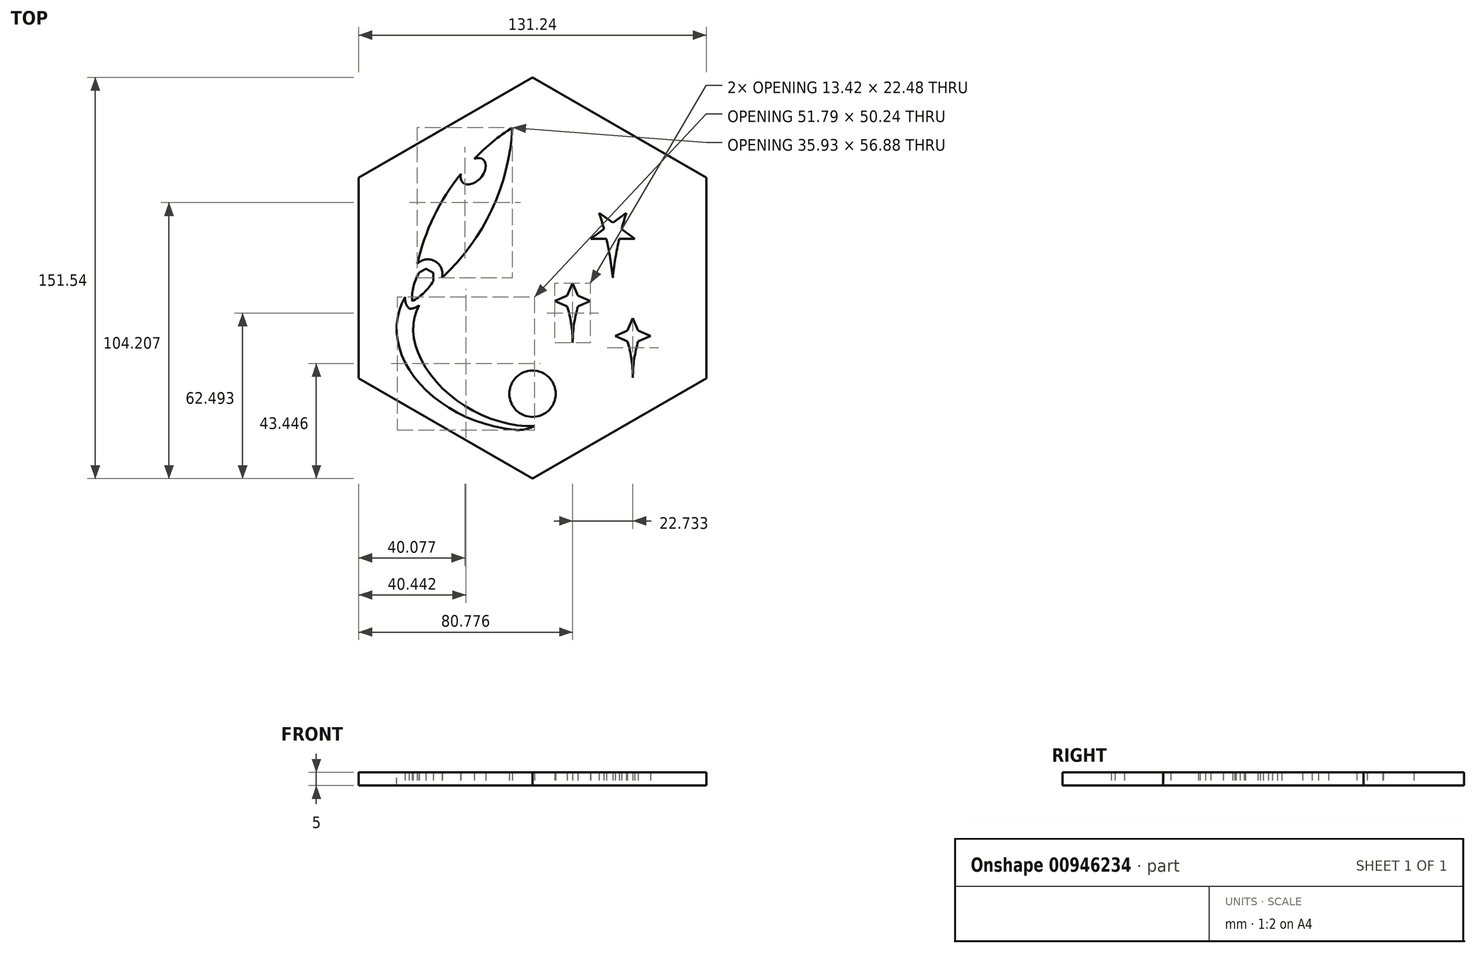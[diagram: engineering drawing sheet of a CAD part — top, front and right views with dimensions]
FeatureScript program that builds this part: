
annotation { "Feature Type Name" : "Feature", "Feature Type Description" : "" }
export const myFeature = defineFeature(function(context is Context, id is Id, definition is map)
    precondition{}
    {
        {
            var Q0;
            Q0=qCreatedBy(makeId("Top.planeOp"),FACE);
            var sketch = newSketch(context, id + "F0", { "sketchPlane" : qUnion([Q0])});
            skCircle(sketch, "E0.cCircle", {"center": v(0, 0) * mm, "radius": 60.62 * mm, "construction": true});
            skLineSegment(sketch, "E0.0", {"start": v(60.62, 35) * mm, "end": v(60.62, -35) * mm});
            skLineSegment(sketch, "E0.1", {"start": v(60.62, -35) * mm, "end": v(0, -70) * mm});
            skLineSegment(sketch, "E0.2", {"start": v(0, -70) * mm, "end": v(-60.62, -35) * mm});
            skLineSegment(sketch, "E0.3", {"start": v(-60.62, -35) * mm, "end": v(-60.62, 35) * mm});
            skLineSegment(sketch, "E0.4", {"start": v(-60.62, 35) * mm, "end": v(0, 70) * mm});
            skLineSegment(sketch, "E0.5", {"start": v(0, 70) * mm, "end": v(60.62, 35) * mm});
            skPoint(sketch, "E0.0.midPoint", {"position": v(60.62, 0) * mm});
            skLineSegment(sketch, "E1", {"start": v(0, 0) * mm, "end": v(0, -35) * mm, "construction": true});
            skLineSegment(sketch, "E2", {"start": v(-30.31, 17.5) * mm, "end": v(-60.62, 35) * mm, "construction": true});
            skLineSegment(sketch, "E3", {"start": v(0, 0) * mm, "end": v(60.62, 35) * mm, "construction": true});
            skLineSegment(sketch, "E4", {"start": v(60.62, -35) * mm, "end": v(15.16, -8.75) * mm, "construction": true});
            skLineSegment(sketch, "E5", {"start": v(0, -35) * mm, "end": v(30.31, 17.5) * mm, "construction": true});
            skLineSegment(sketch, "E6", {"start": v(0, -35) * mm, "end": v(0, -43.75) * mm, "construction": true});
            skLineSegment(sketch, "E7", {"start": v(0, -52.5) * mm, "end": v(0, -70) * mm, "construction": true});
            skLineSegment(sketch, "E8", {"start": v(0, -43.75) * mm, "end": v(0, -52.5) * mm, "construction": true});
            skCircle(sketch, "E9", {"center": v(0, -43.75) * mm, "radius": 8.75 * mm});
            skPoint(sketch, "E10", {"position": v(37.89, -21.88) * mm});
            skPoint(sketch, "E11", {"position": v(-30.31, 17.5) * mm});
            skLineSegment(sketch, "E12", {"start": v(-60.62, -35) * mm, "end": v(-45.47, -8.75) * mm, "construction": true});
            skLineSegment(sketch, "E13", {"start": v(0, 70) * mm, "end": v(-7.58, 56.88) * mm, "construction": true});
            skLineSegment(sketch, "E14", {"start": v(-45.47, -8.75) * mm, "end": v(-37.89, 4.37) * mm, "construction": true});
            skLineSegment(sketch, "E15", {"start": v(-15.16, 43.75) * mm, "end": v(-30.31, 17.5) * mm, "construction": true});
            skLineSegment(sketch, "E16", {"start": v(-7.58, 56.88) * mm, "end": v(-15.16, 43.75) * mm, "construction": true});
            skArc(sketch, "E17", {"start": v(-60.62, -16.52) * mm, "mid": v(-59.59, -16.11) * mm, "end": v(-58.56, -15.69) * mm, "construction": true});
            skLineSegment(sketch, "E18", {"start": v(-15.16, 8.75) * mm, "end": v(-30.31, 17.5) * mm, "construction": true});
            skLineSegment(sketch, "E19", {"start": v(0, 0) * mm, "end": v(-15.16, 8.75) * mm, "construction": true});
            skPoint(sketch, "E20", {"position": v(-22.73, 13.12) * mm});
            skArc(sketch, "E21.trimOffspring", {"start": v(-45.47, -8.75) * mm, "mid": v(-18.65, 19.52) * mm, "end": v(-7.58, 56.88) * mm});
            skArc(sketch, "E22.MirrorCS", {"start": v(-45.47, -8.75) * mm, "mid": v(-34.4, 28.6) * mm, "end": v(-7.58, 56.88) * mm});
            skLineSegment(sketch, "E23", {"start": v(-37.89, 4.37) * mm, "end": v(-34.1, 10.94) * mm, "construction": true});
            skLineSegment(sketch, "E24", {"start": v(-34.1, 10.94) * mm, "end": v(-30.31, 17.5) * mm, "construction": true});
            skCircle(sketch, "E25.cCircle", {"center": v(30.31, 17.5) * mm, "radius": 2.7 * mm, "construction": true});
            skLineSegment(sketch, "E25.0", {"start": v(35.45, 24.58) * mm, "end": v(30.31, 8.75) * mm});
            skLineSegment(sketch, "E25.1", {"start": v(38.63, 14.8) * mm, "end": v(21.99, 14.8) * mm});
            skLineSegment(sketch, "E25.2", {"start": v(30.31, 8.75) * mm, "end": v(25.17, 24.58) * mm});
            skLineSegment(sketch, "E25.3", {"start": v(21.99, 14.8) * mm, "end": v(35.45, 24.58) * mm});
            skLineSegment(sketch, "E25.4", {"start": v(25.17, 24.58) * mm, "end": v(38.63, 14.8) * mm});
            skPoint(sketch, "E25.0.midPoint", {"position": v(32.88, 16.66) * mm});
            skPoint(sketch, "E26.orphan", {"position": v(27.13, 18.53) * mm});
            skPoint(sketch, "E27.orphan", {"position": v(30.31, 20.84) * mm});
            skPoint(sketch, "E28.orphan", {"position": v(33.49, 18.53) * mm});
            skPoint(sketch, "E29.orphan", {"position": v(32.28, 14.8) * mm});
            skPoint(sketch, "E30.orphan", {"position": v(28.35, 14.8) * mm});
            skLineSegment(sketch, "E31", {"start": v(30.31, 17.5) * mm, "end": v(30.31, 0) * mm, "construction": true});
            skPoint(sketch, "E32", {"position": v(30.31, 8.75) * mm});
            skArc(sketch, "E33", {"start": v(30.31, 0) * mm, "mid": v(28.4, 12.43) * mm, "end": v(25.17, 24.58) * mm});
            skArc(sketch, "E34", {"start": v(35.45, 24.58) * mm, "mid": v(32.22, 12.43) * mm, "end": v(30.31, 0) * mm});
            skLineSegment(sketch, "E35", {"start": v(30.31, 17.5) * mm, "end": v(27.97, 18.85) * mm, "construction": true});
            skCircle(sketch, "E36", {"center": v(30.31, 17.5) * mm, "radius": 1.35 * mm, "construction": true});
            skPoint(sketch, "E37", {"position": v(29.14, 18.18) * mm});
            skCircle(sketch, "E38", {"center": v(30.31, 17.5) * mm, "radius": 2.03 * mm, "construction": true});
            skLineSegment(sketch, "E39", {"start": v(30.31, 17.5) * mm, "end": v(30.99, 18.67) * mm, "construction": true});
            skLineSegment(sketch, "E40", {"start": v(30.99, 18.67) * mm, "end": v(31.66, 19.84) * mm, "construction": true});
            skPoint(sketch, "E41", {"position": v(31.32, 19.26) * mm});
            skSolve(sketch);
        }
        {
            var Q0;
            Q0=qCreatedBy(makeId("Top.planeOp"),FACE);
            var sketch = newSketch(context, id + "F1", { "sketchPlane" : qUnion([Q0])});
            skPoint(sketch, "E42.0", {"position": v(15.16, -8.75) * mm});
            skLineSegment(sketch, "E43.0", {"start": v(0, -70) * mm, "end": v(-60.62, -35) * mm});
            skLineSegment(sketch, "E44.0", {"start": v(-60.62, -35) * mm, "end": v(-60.62, 35) * mm});
            skLineSegment(sketch, "E45.0", {"start": v(-60.62, 35) * mm, "end": v(0, 70) * mm});
            skLineSegment(sketch, "E46.0", {"start": v(0, 70) * mm, "end": v(60.62, 35) * mm});
            skLineSegment(sketch, "E47.0", {"start": v(60.62, 35) * mm, "end": v(60.62, -35) * mm});
            skLineSegment(sketch, "E48.0", {"start": v(60.62, -35) * mm, "end": v(0, -70) * mm});
            skArc(sketch, "E49.0", {"start": v(-45.47, -8.75) * mm, "mid": v(-18.65, 19.52) * mm, "end": v(-7.58, 56.88) * mm});
            skArc(sketch, "E50.0", {"start": v(-45.47, -8.75) * mm, "mid": v(-34.4, 28.6) * mm, "end": v(-7.58, 56.88) * mm});
            skCircle(sketch, "E51.cCircle", {"center": v(15.16, -8.75) * mm, "radius": 2.03 * mm, "construction": true});
            skLineSegment(sketch, "E51.3", {"start": v(13.13, -6.72) * mm, "end": v(17.18, -6.72) * mm});
            skPoint(sketch, "E51.0.midPoint", {"position": v(17.18, -8.75) * mm});
            skCircle(sketch, "E52.cCircle", {"center": v(15.16, -5.55) * mm, "radius": 1.17 * mm, "construction": true});
            skLineSegment(sketch, "E52.1", {"start": v(13.13, -6.72) * mm, "end": v(15.16, -3.2) * mm});
            skLineSegment(sketch, "E52.2", {"start": v(15.16, -3.2) * mm, "end": v(17.18, -6.72) * mm});
            skPoint(sketch, "E52.0.midPoint", {"position": v(15.16, -6.72) * mm});
            skLineSegment(sketch, "E53", {"start": v(15.16, -5.55) * mm, "end": v(15.16, -0.87) * mm, "construction": true});
            skPoint(sketch, "E54", {"position": v(15.16, -3.2) * mm});
            skLineSegment(sketch, "E55", {"start": v(15.16, -3.2) * mm, "end": v(15.16, -0.87) * mm, "construction": true});
            skLineSegment(sketch, "E56", {"start": v(17.18, -6.72) * mm, "end": v(15.16, -2.04) * mm});
            skLineSegment(sketch, "E57", {"start": v(13.13, -6.72) * mm, "end": v(15.16, -2.04) * mm});
            skLineSegment(sketch, "E58.1.0", {"start": v(13.13, -6.72) * mm, "end": v(8.44, -8.75) * mm});
            skPoint(sketch, "E58.1.1", {"position": v(13.13, -8.75) * mm});
            skLineSegment(sketch, "E58.1.2", {"start": v(9.62, -8.75) * mm, "end": v(13.13, -6.72) * mm});
            skLineSegment(sketch, "E58.1.3", {"start": v(9.62, -8.75) * mm, "end": v(7.27, -8.75) * mm, "construction": true});
            skLineSegment(sketch, "E58.1.4", {"start": v(11.96, -8.75) * mm, "end": v(7.27, -8.75) * mm, "construction": true});
            skLineSegment(sketch, "E58.1.5", {"start": v(13.13, -10.78) * mm, "end": v(8.44, -8.75) * mm});
            skLineSegment(sketch, "E58.1.6", {"start": v(13.13, -10.78) * mm, "end": v(13.13, -6.72) * mm});
            skCircle(sketch, "E58.1.7", {"center": v(11.96, -8.75) * mm, "radius": 1.17 * mm, "construction": true});
            skPoint(sketch, "E58.1.8", {"position": v(9.62, -8.75) * mm});
            skLineSegment(sketch, "E58.1.9", {"start": v(13.13, -10.78) * mm, "end": v(9.62, -8.75) * mm});
            skLineSegment(sketch, "E58.2.0", {"start": v(13.13, -10.78) * mm, "end": v(15.16, -15.46) * mm});
            skPoint(sketch, "E58.2.1", {"position": v(15.16, -10.78) * mm});
            skLineSegment(sketch, "E58.2.2", {"start": v(15.16, -14.3) * mm, "end": v(13.13, -10.78) * mm});
            skLineSegment(sketch, "E58.2.3", {"start": v(15.16, -14.3) * mm, "end": v(15.16, -16.63) * mm, "construction": true});
            skLineSegment(sketch, "E58.2.4", {"start": v(15.16, -11.95) * mm, "end": v(15.16, -16.63) * mm, "construction": true});
            skLineSegment(sketch, "E58.2.5", {"start": v(17.18, -10.78) * mm, "end": v(15.16, -15.46) * mm});
            skLineSegment(sketch, "E58.2.6", {"start": v(17.18, -10.78) * mm, "end": v(13.13, -10.78) * mm});
            skCircle(sketch, "E58.2.7", {"center": v(15.16, -11.95) * mm, "radius": 1.17 * mm, "construction": true});
            skPoint(sketch, "E58.2.8", {"position": v(15.16, -14.3) * mm});
            skLineSegment(sketch, "E58.2.9", {"start": v(17.18, -10.78) * mm, "end": v(15.16, -14.3) * mm});
            skLineSegment(sketch, "E58.3.0", {"start": v(17.18, -10.78) * mm, "end": v(21.87, -8.75) * mm});
            skLineSegment(sketch, "E58.3.2", {"start": v(20.7, -8.75) * mm, "end": v(17.18, -10.78) * mm});
            skLineSegment(sketch, "E58.3.3", {"start": v(20.7, -8.75) * mm, "end": v(23.04, -8.75) * mm, "construction": true});
            skLineSegment(sketch, "E58.3.4", {"start": v(18.35, -8.75) * mm, "end": v(23.04, -8.75) * mm, "construction": true});
            skLineSegment(sketch, "E58.3.5", {"start": v(17.18, -6.72) * mm, "end": v(21.87, -8.75) * mm});
            skLineSegment(sketch, "E58.3.6", {"start": v(17.18, -6.72) * mm, "end": v(17.18, -10.78) * mm});
            skCircle(sketch, "E58.3.7", {"center": v(18.35, -8.75) * mm, "radius": 1.17 * mm, "construction": true});
            skPoint(sketch, "E58.3.8", {"position": v(20.7, -8.75) * mm});
            skLineSegment(sketch, "E58.3.9", {"start": v(17.18, -6.72) * mm, "end": v(20.7, -8.75) * mm});
            skLineSegment(sketch, "E59", {"start": v(15.16, -8.75) * mm, "end": v(15.16, -24.51) * mm, "construction": true});
            skArc(sketch, "E60", {"start": v(17.18, -10.78) * mm, "mid": v(15.67, -17.57) * mm, "end": v(15.16, -24.51) * mm});
            skArc(sketch, "E61", {"start": v(15.16, -24.51) * mm, "mid": v(14.65, -17.57) * mm, "end": v(13.13, -10.78) * mm});
            skPoint(sketch, "E62.0", {"position": v(37.89, -21.88) * mm});
            skCircle(sketch, "E63.cCircle", {"center": v(37.89, -21.88) * mm, "radius": 2.03 * mm, "construction": true});
            skLineSegment(sketch, "E63.0", {"start": v(39.92, -19.85) * mm, "end": v(39.92, -23.9) * mm});
            skLineSegment(sketch, "E63.1", {"start": v(39.92, -23.9) * mm, "end": v(35.86, -23.9) * mm});
            skLineSegment(sketch, "E63.2", {"start": v(35.86, -23.9) * mm, "end": v(35.86, -19.85) * mm});
            skLineSegment(sketch, "E63.3", {"start": v(35.86, -19.85) * mm, "end": v(39.92, -19.85) * mm});
            skPoint(sketch, "E63.0.midPoint", {"position": v(39.92, -21.88) * mm});
            skCircle(sketch, "E64.cCircle", {"center": v(37.89, -18.68) * mm, "radius": 1.17 * mm, "construction": true});
            skLineSegment(sketch, "E64.0", {"start": v(35.86, -19.85) * mm, "end": v(37.89, -16.33) * mm});
            skLineSegment(sketch, "E64.1", {"start": v(37.89, -16.33) * mm, "end": v(39.92, -19.85) * mm});
            skLineSegment(sketch, "E64.2", {"start": v(39.92, -19.85) * mm, "end": v(35.86, -19.85) * mm});
            skPoint(sketch, "E64.0.midPoint", {"position": v(36.87, -18.1) * mm});
            skLineSegment(sketch, "E65", {"start": v(37.89, -18.68) * mm, "end": v(37.89, -14) * mm, "construction": true});
            skLineSegment(sketch, "E66", {"start": v(37.89, -16.33) * mm, "end": v(37.89, -14) * mm, "construction": true});
            skLineSegment(sketch, "E67", {"start": v(39.92, -19.85) * mm, "end": v(37.89, -15.16) * mm});
            skLineSegment(sketch, "E68", {"start": v(35.86, -19.85) * mm, "end": v(37.89, -15.16) * mm});
            skLineSegment(sketch, "E69.1.0", {"start": v(35.86, -23.9) * mm, "end": v(32.35, -21.87) * mm});
            skLineSegment(sketch, "E69.1.1", {"start": v(34.69, -21.87) * mm, "end": v(30, -21.88) * mm, "construction": true});
            skLineSegment(sketch, "E69.1.2", {"start": v(32.35, -21.88) * mm, "end": v(35.86, -19.85) * mm});
            skLineSegment(sketch, "E69.1.3", {"start": v(32.35, -21.88) * mm, "end": v(30, -21.88) * mm, "construction": true});
            skLineSegment(sketch, "E69.1.4", {"start": v(35.86, -23.9) * mm, "end": v(31.18, -21.88) * mm});
            skPoint(sketch, "E69.1.5", {"position": v(34.1, -22.89) * mm});
            skLineSegment(sketch, "E69.1.6", {"start": v(35.86, -19.85) * mm, "end": v(35.86, -23.9) * mm});
            skCircle(sketch, "E69.1.7", {"center": v(34.69, -21.87) * mm, "radius": 1.17 * mm, "construction": true});
            skLineSegment(sketch, "E69.1.8", {"start": v(35.86, -19.85) * mm, "end": v(31.18, -21.88) * mm});
            skLineSegment(sketch, "E69.2.0", {"start": v(39.92, -23.9) * mm, "end": v(37.89, -27.42) * mm});
            skLineSegment(sketch, "E69.2.1", {"start": v(37.89, -25.07) * mm, "end": v(37.89, -29.76) * mm, "construction": true});
            skLineSegment(sketch, "E69.2.2", {"start": v(37.89, -27.42) * mm, "end": v(35.86, -23.9) * mm});
            skLineSegment(sketch, "E69.2.3", {"start": v(37.89, -27.42) * mm, "end": v(37.89, -29.76) * mm, "construction": true});
            skLineSegment(sketch, "E69.2.4", {"start": v(39.92, -23.9) * mm, "end": v(37.89, -28.59) * mm});
            skPoint(sketch, "E69.2.5", {"position": v(38.9, -25.66) * mm});
            skLineSegment(sketch, "E69.2.6", {"start": v(35.86, -23.9) * mm, "end": v(39.92, -23.9) * mm});
            skCircle(sketch, "E69.2.7", {"center": v(37.89, -25.07) * mm, "radius": 1.17 * mm, "construction": true});
            skLineSegment(sketch, "E69.2.8", {"start": v(35.86, -23.9) * mm, "end": v(37.89, -28.59) * mm});
            skLineSegment(sketch, "E69.3.0", {"start": v(39.92, -19.85) * mm, "end": v(43.43, -21.88) * mm});
            skLineSegment(sketch, "E69.3.1", {"start": v(41.09, -21.88) * mm, "end": v(45.77, -21.87) * mm, "construction": true});
            skLineSegment(sketch, "E69.3.2", {"start": v(43.43, -21.87) * mm, "end": v(39.92, -23.9) * mm});
            skLineSegment(sketch, "E69.3.3", {"start": v(43.43, -21.87) * mm, "end": v(45.77, -21.87) * mm, "construction": true});
            skLineSegment(sketch, "E69.3.4", {"start": v(39.92, -19.85) * mm, "end": v(44.6, -21.88) * mm});
            skPoint(sketch, "E69.3.5", {"position": v(41.67, -20.86) * mm});
            skLineSegment(sketch, "E69.3.6", {"start": v(39.92, -23.9) * mm, "end": v(39.92, -19.85) * mm});
            skCircle(sketch, "E69.3.7", {"center": v(41.09, -21.88) * mm, "radius": 1.17 * mm, "construction": true});
            skLineSegment(sketch, "E69.3.8", {"start": v(39.92, -23.9) * mm, "end": v(44.6, -21.87) * mm});
            skLineSegment(sketch, "E70", {"start": v(37.89, -21.88) * mm, "end": v(37.89, -37.64) * mm, "construction": true});
            skSolve(sketch);
        }
        {
            var Q0;
            Q0=makeQuery(id+"F0.imprint","IMPRINT",FACE,{"disambiguationData":[TD([[makeQuery(id+"F0.imprint","IMPRINT",EDGE,{"derivedFrom":sQuery(id+"F0.wireOp",EDGE,"E0.0")}),-1.0]])]});
            var sketch = newSketch(context, id + "F2", { "sketchPlane" : qUnion([Q0])});
            skPoint(sketch, "E71.0", {"position": v(35.86, -23.9) * mm});
            skPoint(sketch, "E72.0", {"position": v(39.92, -23.9) * mm});
            skPoint(sketch, "E73.0", {"position": v(37.89, -37.64) * mm});
            skArc(sketch, "E74", {"start": v(37.89, -37.64) * mm, "mid": v(37.38, -30.7) * mm, "end": v(35.86, -23.9) * mm});
            skLineSegment(sketch, "E75.0", {"start": v(37.89, -21.88) * mm, "end": v(37.89, -37.64) * mm, "construction": true});
            skArc(sketch, "E76", {"start": v(39.92, -23.9) * mm, "mid": v(38.4, -30.7) * mm, "end": v(37.89, -37.64) * mm});
            skSolve(sketch);
        }
        {
            var Q0;
            Q0=makeQuery(id+"F0.imprint","IMPRINT",FACE,{"disambiguationData":[TD([[makeQuery(id+"F0.imprint","IMPRINT",EDGE,{"derivedFrom":sQuery(id+"F0.wireOp",EDGE,"E0.0")}),-1.0]])]});
            var sketch = newSketch(context, id + "F3", { "sketchPlane" : qUnion([Q0])});
            skArc(sketch, "E77.0", {"start": v(-43.5, 5.36) * mm, "mid": v(-30.57, 34.63) * mm, "end": v(-7.58, 56.88) * mm});
            skArc(sketch, "E77.1", {"start": v(-34.23, 0) * mm, "mid": v(-15.35, 25.84) * mm, "end": v(-7.58, 56.88) * mm});
            skArc(sketch, "E78", {"start": v(-34.23, 0) * mm, "mid": v(-36.78, 6.3) * mm, "end": v(-43.5, 5.36) * mm});
            skLineSegment(sketch, "E79", {"start": v(-34.23, 0) * mm, "end": v(-36.55, 1.34) * mm, "construction": true});
            skLineSegment(sketch, "E80", {"start": v(-38.87, 2.68) * mm, "end": v(-43.5, 5.36) * mm, "construction": true});
            skLineSegment(sketch, "E81", {"start": v(-36.55, 1.34) * mm, "end": v(-38.87, 2.68) * mm, "construction": true});
            skLineSegment(sketch, "E82", {"start": v(-38.87, 2.68) * mm, "end": v(-40.2, 0.36) * mm, "construction": true});
            skPoint(sketch, "E83.orphan", {"position": v(-45.47, -8.75) * mm});
            skCircle(sketch, "E84.cCircle", {"center": v(-40.2, 0.36) * mm, "radius": 2.68 * mm, "construction": true});
            skLineSegment(sketch, "E84.2", {"start": v(-42.89, 1.9) * mm, "end": v(-40.2, 3.45) * mm});
            skLineSegment(sketch, "E84.3", {"start": v(-40.2, 3.45) * mm, "end": v(-37.53, 1.9) * mm});
            skLineSegment(sketch, "E84.4", {"start": v(-37.53, 1.9) * mm, "end": v(-37.53, -1.19) * mm});
            skPoint(sketch, "E84.0.midPoint", {"position": v(-41.55, -1.96) * mm});
            skArc(sketch, "E85", {"start": v(-45.47, -8.75) * mm, "mid": v(-40.95, -5.54) * mm, "end": v(-37.53, -1.19) * mm, "construction": true});
            skArc(sketch, "E86.MirrorCS", {"start": v(-45.47, -8.75) * mm, "mid": v(-44.94, -3.24) * mm, "end": v(-42.89, 1.9) * mm, "construction": true});
            skLineSegment(sketch, "E87", {"start": v(-36.22, 1.9) * mm, "end": v(-42.37, -8.75) * mm, "construction": true});
            skLineSegment(sketch, "E88", {"start": v(-35.74, 1.9) * mm, "end": v(-41.9, -8.75) * mm, "construction": true});
            skCircle(sketch, "E89.0", {"center": v(0, -43.75) * mm, "radius": 8.75 * mm});
            skLineSegment(sketch, "E90", {"start": v(0, -43.75) * mm, "end": v(-8.75, -43.75) * mm, "construction": true});
            skLineSegment(sketch, "E91", {"start": v(-17.5, -43.75) * mm, "end": v(-8.75, -43.75) * mm, "construction": true});
            skPoint(sketch, "E92", {"position": v(-44.94, -3.24) * mm});
            skPoint(sketch, "E93", {"position": v(-40.95, -5.54) * mm});
            skLineSegment(sketch, "E94", {"start": v(-48.15, -7.2) * mm, "end": v(-45.47, -8.75) * mm, "construction": true});
            skLineSegment(sketch, "E95", {"start": v(-37.53, -1.19) * mm, "end": v(-42.79, -10.3) * mm, "construction": true});
            skLineSegment(sketch, "E96", {"start": v(0, -43.75) * mm, "end": v(0, -52.5) * mm, "construction": true});
            skLineSegment(sketch, "E97", {"start": v(0, -43.75) * mm, "end": v(-6.19, -49.94) * mm, "construction": true});
            skLineSegment(sketch, "E98", {"start": v(0, -52.5) * mm, "end": v(-8.75, -43.75) * mm, "construction": true});
            skPoint(sketch, "E99", {"position": v(-4.38, -48.13) * mm});
            skLineSegment(sketch, "E100", {"start": v(0, -43.75) * mm, "end": v(-16.17, -50.45) * mm, "construction": true});
            skLineSegment(sketch, "E101", {"start": v(-6.19, -49.94) * mm, "end": v(-8.75, -43.75) * mm, "construction": true});
            skPoint(sketch, "E102", {"position": v(-7.47, -46.84) * mm});
            skCircle(sketch, "E103", {"center": v(0, -43.75) * mm, "radius": 17.5 * mm, "construction": true});
            skLineSegment(sketch, "E104", {"start": v(-16.17, -50.45) * mm, "end": v(-16.83, -47.1) * mm, "construction": true});
            skPoint(sketch, "E105", {"position": v(-16.83, -47.1) * mm});
            skLineSegment(sketch, "E106", {"start": v(0, -43.75) * mm, "end": v(-12.63, -46.26) * mm, "construction": true});
            skLineSegment(sketch, "E107", {"start": v(-45.47, -8.75) * mm, "end": v(-44.94, -3.24) * mm, "construction": true});
            skLineSegment(sketch, "E108", {"start": v(-40.95, -5.54) * mm, "end": v(-45.47, -8.75) * mm, "construction": true});
            skPoint(sketch, "E109", {"position": v(-45.2, -6) * mm});
            skPoint(sketch, "E110", {"position": v(-43.2, -7.15) * mm});
            skLineSegment(sketch, "E111", {"start": v(-13.13, -43.75) * mm, "end": v(-12.63, -46.26) * mm, "construction": true});
            skPoint(sketch, "E112.0", {"position": v(-15.16, 43.75) * mm});
            skPoint(sketch, "E113.0", {"position": v(-30.31, 17.5) * mm});
            skLineSegment(sketch, "E114", {"start": v(-15.16, 43.75) * mm, "end": v(-18.94, 37.19) * mm, "construction": true});
            skLineSegment(sketch, "E115", {"start": v(-22.73, 30.62) * mm, "end": v(-30.31, 17.5) * mm, "construction": true});
            skLineSegment(sketch, "E116", {"start": v(-18.94, 37.19) * mm, "end": v(-22.73, 30.62) * mm, "construction": true});
            skEllipse(sketch, "E117", {"center": v(-22.42, 40.3) * mm, "majorRadius": 5.8 * mm, "minorRadius": 4.67 * mm, "majorAxis": v(0.67, 0.74), "construction": true});
            skPoint(sketch, "E118", {"position": v(-26.3, 35.97) * mm});
            skPoint(sketch, "E119", {"position": v(-18.55, 44.63) * mm});
            skLineSegment(sketch, "E120", {"start": v(-7.58, 56.88) * mm, "end": v(-27.47, 31.17) * mm, "construction": true});
            skEllipse(sketch, "E121", {"center": v(-22.73, 30.62) * mm, "majorRadius": 8.74 * mm, "minorRadius": 3.79 * mm, "majorAxis": v(0.87, -0.5), "construction": true});
            skPoint(sketch, "E122", {"position": v(-24.63, 27.34) * mm});
            skPoint(sketch, "E123", {"position": v(-30.3, 35) * mm});
            skLineSegment(sketch, "E124", {"start": v(-30.3, 35) * mm, "end": v(-27.47, 31.17) * mm, "construction": true});
            skPoint(sketch, "E125", {"position": v(-27.47, 31.17) * mm});
            skPoint(sketch, "E126", {"position": v(-20.84, 33.9) * mm});
            skPoint(sketch, "E127", {"position": v(-25.9, 43.42) * mm});
            skLineSegment(sketch, "E128", {"start": v(-27.47, 31.17) * mm, "end": v(-24.63, 27.34) * mm, "construction": true});
            skPoint(sketch, "E129", {"position": v(-28.89, 33.08) * mm});
            skLineSegment(sketch, "E130", {"start": v(-7.58, 56.88) * mm, "end": v(-28.89, 33.08) * mm, "construction": true});
            skPoint(sketch, "E131", {"position": v(-18.94, 37.19) * mm});
            skLineSegment(sketch, "E132", {"start": v(-45.47, -8.75) * mm, "end": v(-42.79, -10.3) * mm, "construction": true});
            skLineSegment(sketch, "E133", {"start": v(-16.83, -47.1) * mm, "end": v(-17.5, -43.75) * mm, "construction": true});
            skPoint(sketch, "E134", {"position": v(-17.17, -45.42) * mm});
            skPoint(sketch, "E135", {"position": v(-12.88, -45) * mm});
            skLineSegment(sketch, "E136", {"start": v(-12.88, -45) * mm, "end": v(-17.17, -45.42) * mm, "construction": true});
            skLineSegment(sketch, "E137", {"start": v(-12.63, -46.26) * mm, "end": v(-17.16, -47.16) * mm, "construction": true});
            skLineSegment(sketch, "E138", {"start": v(-13.13, -43.75) * mm, "end": v(-17.5, -43.75) * mm, "construction": true});
            skPoint(sketch, "E139", {"position": v(-15.31, -43.75) * mm});
            skPoint(sketch, "E140", {"position": v(-14.9, -46.71) * mm});
            skLineSegment(sketch, "E141", {"start": v(-14.9, -46.71) * mm, "end": v(-15.02, -45.21) * mm, "construction": true});
            skPoint(sketch, "E142", {"position": v(-14.96, -45.96) * mm});
            skArc(sketch, "E143", {"start": v(-17.17, -45.42) * mm, "mid": v(-16.01, -45.5) * mm, "end": v(-14.96, -45.96) * mm, "construction": true});
            skArc(sketch, "E144", {"start": v(-16.83, -47.1) * mm, "mid": v(-15.8, -46.7) * mm, "end": v(-14.96, -45.96) * mm, "construction": true});
            skPoint(sketch, "E145", {"position": v(-40.3, -35.38) * mm});
            skLineSegment(sketch, "E146", {"start": v(-40.3, -35.38) * mm, "end": v(-43.78, -37.93) * mm, "construction": true});
            skPoint(sketch, "E147", {"position": v(-42.04, -36.66) * mm});
            skArc(sketch, "E148", {"start": v(-45.47, -8.75) * mm, "mid": v(-41.85, -36.9) * mm, "end": v(-14.96, -45.96) * mm, "construction": true});
            skLineSegment(sketch, "E149", {"start": v(-46.6, -11.63) * mm, "end": v(-45.47, -8.75) * mm, "construction": true});
            skLineSegment(sketch, "E150", {"start": v(-45.47, -8.75) * mm, "end": v(-46.49, -5.83) * mm, "construction": true});
            skArc(sketch, "E151", {"start": v(-48.15, -7.2) * mm, "mid": v(-44.74, -36.77) * mm, "end": v(-16.83, -47.1) * mm, "construction": true});
            skArc(sketch, "E152", {"start": v(-42.79, -10.3) * mm, "mid": v(-40.3, -35.38) * mm, "end": v(-17.17, -45.42) * mm, "construction": true});
            skArc(sketch, "E153", {"start": v(-48.15, -7.2) * mm, "mid": v(-47.84, -9.58) * mm, "end": v(-46.6, -11.63) * mm});
            skArc(sketch, "E154", {"start": v(-46.6, -11.63) * mm, "mid": v(-44.57, -11.3) * mm, "end": v(-42.79, -10.3) * mm});
            skLineSegment(sketch, "E155", {"start": v(0, -52.5) * mm, "end": v(0, -61.25) * mm, "construction": true});
            skPoint(sketch, "E156", {"position": v(0, -56.88) * mm});
            skCircle(sketch, "E157", {"center": v(0, -45.94) * mm, "radius": 10.94 * mm, "construction": true});
            skArc(sketch, "E158", {"start": v(-40.2, 0.36) * mm, "mid": v(-34.97, -38.7) * mm, "end": v(0, -56.88) * mm, "construction": true});
            skCircle(sketch, "E159", {"center": v(-40.2, 0.36) * mm, "radius": 10.52 * mm, "construction": true});
            skArc(sketch, "E160", {"start": v(-42.89, 1.9) * mm, "mid": v(-43.62, -4) * mm, "end": v(-42.52, -9.84) * mm});
            skArc(sketch, "E161", {"start": v(-42.52, -9.84) * mm, "mid": v(-39.46, -5.84) * mm, "end": v(-37.53, -1.19) * mm});
            skEllipse(sketch, "E162", {"center": v(-22.42, 40.3) * mm, "majorRadius": 5.8 * mm, "minorRadius": 3.78 * mm, "majorAxis": v(0.67, 0.74)});
            skLineSegment(sketch, "E163", {"start": v(-25.9, 43.42) * mm, "end": v(-24.58, 42.24) * mm, "construction": true});
            skPoint(sketch, "E164", {"position": v(-25.24, 42.83) * mm});
            skLineSegment(sketch, "E165.MirrorCS", {"start": v(-18.94, 37.19) * mm, "end": v(-20.26, 38.37) * mm, "construction": true});
            skPoint(sketch, "E166.MirrorP", {"position": v(-19.6, 37.78) * mm});
            skSolve(sketch);
        }
        {
            var Q0;
            Q0=qCreatedBy(makeId("Top.planeOp"),FACE);
            var sketch = newSketch(context, id + "F4", { "sketchPlane" : qUnion([Q0])});
            skCircle(sketch, "E167.0", {"center": v(0, -43.75) * mm, "radius": 8.75 * mm, "construction": true});
            skPoint(sketch, "E168.0", {"position": v(-48.15, -7.2) * mm});
            skPoint(sketch, "E169.0", {"position": v(-42.79, -10.3) * mm});
            skLineSegment(sketch, "E170", {"start": v(0, -43.75) * mm, "end": v(0, -52.5) * mm, "construction": true});
            skLineSegment(sketch, "E171", {"start": v(0, -52.5) * mm, "end": v(0, -56.88) * mm, "construction": true});
            skLineSegment(sketch, "E172", {"start": v(0, -56.88) * mm, "end": v(0, -61.25) * mm, "construction": true});
            skLineSegment(sketch, "E173.0", {"start": v(-12.88, -45) * mm, "end": v(-15.02, -45.21) * mm, "construction": true});
            skLineSegment(sketch, "E174", {"start": v(-15.02, -45.21) * mm, "end": v(-17.17, -45.42) * mm, "construction": true});
            skLineSegment(sketch, "E175", {"start": v(0, -43.75) * mm, "end": v(-2.85, -61.02) * mm, "construction": true});
            skCircle(sketch, "E176.0", {"center": v(0, -43.75) * mm, "radius": 17.5 * mm, "construction": true});
            skLineSegment(sketch, "E177", {"start": v(0, -56.88) * mm, "end": v(-2.16, -56.82) * mm, "construction": true});
            skArc(sketch, "E178", {"start": v(-45.47, -8.75) * mm, "mid": v(-33.1, -42.6) * mm, "end": v(0, -56.88) * mm, "construction": true});
            skPoint(sketch, "E179.0", {"position": v(-45.47, -8.75) * mm});
            skLineSegment(sketch, "E180.0", {"start": v(-16.83, -47.1) * mm, "end": v(-17.17, -45.42) * mm, "construction": true});
            skLineSegment(sketch, "E181", {"start": v(-17.17, -45.42) * mm, "end": v(-17.5, -43.75) * mm, "construction": true});
            skLineSegment(sketch, "E182", {"start": v(-2.12, -55.97) * mm, "end": v(-2.2, -57.68) * mm, "construction": true});
            skPoint(sketch, "E183", {"position": v(-2.16, -56.82) * mm});
            skArc(sketch, "E184", {"start": v(0, -56.88) * mm, "mid": v(-0.97, -56.23) * mm, "end": v(-2.12, -55.97) * mm, "construction": true});
            skArc(sketch, "E185", {"start": v(-2.2, -57.68) * mm, "mid": v(-1.02, -57.48) * mm, "end": v(0, -56.88) * mm});
            skCircle(sketch, "E186", {"center": v(0, -45.94) * mm, "radius": 10.94 * mm, "construction": true});
            skLineSegment(sketch, "E187", {"start": v(-45.54, -11.84) * mm, "end": v(-45.47, -8.75) * mm, "construction": true});
            skLineSegment(sketch, "E188", {"start": v(-48.15, -7.2) * mm, "end": v(-44.78, -1.37) * mm, "construction": true});
            skPoint(sketch, "E189", {"position": v(-16.83, -55.46) * mm});
            skEllipticalArc(sketch, "E190", {});
            skEllipticalArc(sketch, "E191", {"construction": true});
            skEllipticalArc(sketch, "E192", {});
            skEllipticalArc(sketch, "E193", {"construction": true});
            skArc(sketch, "E194.0", {"start": v(-46.6, -11.63) * mm, "mid": v(-44.57, -11.3) * mm, "end": v(-42.79, -10.3) * mm});
            skArc(sketch, "E195.0", {"start": v(-48.15, -7.2) * mm, "mid": v(-47.84, -9.58) * mm, "end": v(-46.6, -11.63) * mm});
            const initialGuessF4  = {"E190": [-0.008122247099933005, -0.02456963054964719, 0.9624687106606815, -0.2713926693909868, 0.0439718499911378, 0.032099978341677673, 2.958237406010736, 5.052989680657434], "E191": [-0.008122247099933005, -0.02456963054964719, 0.9624687106606815, -0.2713926693909868, 0.0439718499911378, 0.032099978341677673, 5.052989680657434, 2.9582374060107366], "E192": [-0.011639922779706047, -0.02827968744979026, -0.8660254037844389, 0.5, 0.03596520862109229, 0.024357615432259415, 0, 2.2323374718868], "E193": [-0.011639922779706047, -0.02827968744979026, -0.8660254037844389, 0.5, 0.03596520862109229, 0.024357615432259415, 2.2323374718868, 0]};
            skSetInitialGuess(sketch, initialGuessF4);
            skSolve(sketch);
        }
        {
            var Q0;
            Q0=qCreatedBy(makeId("Top.planeOp"),FACE);
            var sketch = newSketch(context, id + "F5", { "sketchPlane" : qUnion([Q0])});
            skEllipticalArc(sketch, "E196.0", {});
            skArc(sketch, "E197.0", {"start": v(-2.2, -57.68) * mm, "mid": v(-0.5, -57.24) * mm, "end": v(0.72, -55.97) * mm, "construction": true});
            skEllipticalArc(sketch, "E198.0", {});
            skPoint(sketch, "E199.orphan", {"position": v(0, -56.88) * mm});
            skEllipticalArc(sketch, "E200", {"construction": true});
            skEllipticalArc(sketch, "E201.1", {});
            skArc(sketch, "E202", {"start": v(-6.91, -57.38) * mm, "mid": v(-3, -57.22) * mm, "end": v(0.72, -55.97) * mm});
            skEllipticalArc(sketch, "E203", {"construction": true});
            skArc(sketch, "E204.0", {"start": v(-48.15, -7.2) * mm, "mid": v(-47.84, -9.58) * mm, "end": v(-46.6, -11.63) * mm});
            skArc(sketch, "E205.0", {"start": v(-46.6, -11.63) * mm, "mid": v(-44.57, -11.3) * mm, "end": v(-42.79, -10.3) * mm});
            const initialGuessF5  = {"E196.0": [-0.011639922779706047, -0.02827968744979026, -0.8660254037844389, 0.5, 0.03596520862109229, 0.024357615432259415, 0, 2.2323374718868], "E198.0": [-0.011639922779706047, -0.02827968744979026, -0.8660254037844389, 0.5, 0.03596520862109229, 0.024357615432259415, 2.2323374718868, 2.3219350337154445], "E200": [-0.011639922779706047, -0.02827968744979026, -0.8660254037844389, 0.5, 0.03596520862109229, 0.024357615432259415, 2.3219350337154445, 0], "E201.1": [-0.008122247099933005, -0.02456963054964719, 0.9624687106606815, -0.2713926693909868, 0.0439718499911378, 0.032099978341677673, 2.958237406010736, 4.943351541940011], "E203": [-0.008122247099933005, -0.02456963054964719, 0.9624687106606815, -0.2713926693909868, 0.0439718499911378, 0.032099978341677673, 4.943351541940011, 5.052989680657434]};
            skSetInitialGuess(sketch, initialGuessF5);
            skSolve(sketch);
        }
        {
            var Q0;
            Q0=qCreatedBy(makeId("Top.planeOp"),FACE);
            var sketch = newSketch(context, id + "F6", { "sketchPlane" : qUnion([Q0])});
            skCircle(sketch, "E206.0", {"center": v(0, -43.75) * mm, "radius": 8.75 * mm});
            skLineSegment(sketch, "E207.0", {"start": v(60.62, -35) * mm, "end": v(0, -70) * mm, "construction": true});
            skArc(sketch, "E208.0", {"start": v(-34.23, 0) * mm, "mid": v(-15.35, 25.84) * mm, "end": v(-7.58, 56.88) * mm});
            skArc(sketch, "E209.0", {"start": v(-34.23, 0) * mm, "mid": v(-36.78, 6.3) * mm, "end": v(-43.5, 5.36) * mm});
            skLineSegment(sketch, "E210.0", {"start": v(-42.89, 1.9) * mm, "end": v(-40.2, 3.45) * mm});
            skArc(sketch, "E211.0", {"start": v(-45.47, -8.75) * mm, "mid": v(-44.94, -3.24) * mm, "end": v(-42.89, 1.9) * mm});
            skLineSegment(sketch, "E212.0", {"start": v(-40.2, 3.45) * mm, "end": v(-37.53, 1.9) * mm});
            skLineSegment(sketch, "E213.0", {"start": v(-37.53, 1.9) * mm, "end": v(-37.53, -1.19) * mm});
            skArc(sketch, "E214.0", {"start": v(-45.47, -8.75) * mm, "mid": v(-40.95, -5.54) * mm, "end": v(-37.53, -1.19) * mm});
            skArc(sketch, "E215.0", {"start": v(15.16, -24.51) * mm, "mid": v(14.65, -17.57) * mm, "end": v(13.13, -10.78) * mm});
            skArc(sketch, "E216.0", {"start": v(17.18, -10.78) * mm, "mid": v(15.67, -17.57) * mm, "end": v(15.16, -24.51) * mm});
            skLineSegment(sketch, "E217.0", {"start": v(17.18, -10.78) * mm, "end": v(21.87, -8.75) * mm});
            skLineSegment(sketch, "E218.0", {"start": v(17.18, -6.72) * mm, "end": v(21.87, -8.75) * mm});
            skLineSegment(sketch, "E219.0", {"start": v(17.18, -6.72) * mm, "end": v(15.16, -2.04) * mm});
            skLineSegment(sketch, "E220.0", {"start": v(13.13, -6.72) * mm, "end": v(15.16, -2.04) * mm});
            skLineSegment(sketch, "E221.0", {"start": v(13.13, -6.72) * mm, "end": v(8.44, -8.75) * mm});
            skLineSegment(sketch, "E222.0", {"start": v(13.13, -10.78) * mm, "end": v(8.44, -8.75) * mm});
            skArc(sketch, "E223.0", {"start": v(39.92, -23.9) * mm, "mid": v(38.4, -30.7) * mm, "end": v(37.89, -37.64) * mm});
            skArc(sketch, "E224.0", {"start": v(37.89, -37.64) * mm, "mid": v(37.38, -30.7) * mm, "end": v(35.86, -23.9) * mm});
            skLineSegment(sketch, "E225.0", {"start": v(35.86, -23.9) * mm, "end": v(31.18, -21.88) * mm});
            skLineSegment(sketch, "E226.0", {"start": v(35.86, -19.85) * mm, "end": v(31.18, -21.88) * mm});
            skLineSegment(sketch, "E227.0", {"start": v(35.86, -19.85) * mm, "end": v(37.89, -15.16) * mm});
            skLineSegment(sketch, "E228.0", {"start": v(39.92, -19.85) * mm, "end": v(37.89, -15.16) * mm});
            skLineSegment(sketch, "E229.0", {"start": v(39.92, -19.85) * mm, "end": v(44.6, -21.88) * mm});
            skLineSegment(sketch, "E230.0", {"start": v(39.92, -23.9) * mm, "end": v(44.6, -21.87) * mm});
            skLineSegment(sketch, "E231.0", {"start": v(21.99, 14.8) * mm, "end": v(26.98, 18.42) * mm});
            skLineSegment(sketch, "E232.0", {"start": v(25.17, 24.58) * mm, "end": v(30.31, 20.84) * mm});
            skArc(sketch, "E233.0", {"start": v(30.31, 0) * mm, "mid": v(29.33, 7.44) * mm, "end": v(27.88, 14.8) * mm});
            skArc(sketch, "E234.0", {"start": v(35.45, 24.58) * mm, "mid": v(34.5, 21.51) * mm, "end": v(33.64, 18.42) * mm});
            skLineSegment(sketch, "E235.0", {"start": v(38.63, 14.8) * mm, "end": v(32.74, 14.8) * mm});
            skLineSegment(sketch, "E236.trimOffspring", {"start": v(27.88, 14.8) * mm, "end": v(21.99, 14.8) * mm});
            skArc(sketch, "E237.trimOffspring", {"start": v(26.98, 18.42) * mm, "mid": v(26.12, 21.51) * mm, "end": v(25.17, 24.58) * mm});
            skLineSegment(sketch, "E238.trimOffspring", {"start": v(30.31, 20.84) * mm, "end": v(35.45, 24.58) * mm});
            skLineSegment(sketch, "E239.trimOffspring", {"start": v(33.64, 18.42) * mm, "end": v(38.63, 14.8) * mm});
            skArc(sketch, "E240.trimOffspring", {"start": v(32.74, 14.8) * mm, "mid": v(31.29, 7.44) * mm, "end": v(30.31, 0) * mm});
            skLineSegment(sketch, "E241.0.2", {"start": v(-60.62, 35) * mm, "end": v(-60.62, -35) * mm, "construction": true});
            skLineSegment(sketch, "E241.0.5", {"start": v(60.62, -35) * mm, "end": v(60.62, 35) * mm, "construction": true});
            skLineSegment(sketch, "E242.0.0", {"start": v(60.62, 35) * mm, "end": v(0, 70) * mm, "construction": true});
            skLineSegment(sketch, "E242.0.1", {"start": v(0, 70) * mm, "end": v(-60.62, 35) * mm, "construction": true});
            skLineSegment(sketch, "E242.0.3", {"start": v(-60.62, -35) * mm, "end": v(0, -70) * mm, "construction": true});
            skArc(sketch, "E243.0", {"start": v(-48.15, -7.2) * mm, "mid": v(-47.84, -9.58) * mm, "end": v(-46.6, -11.63) * mm});
            skArc(sketch, "E244.0", {"start": v(-46.6, -11.63) * mm, "mid": v(-44.57, -11.3) * mm, "end": v(-42.79, -10.3) * mm});
            skLineSegment(sketch, "E245.0", {"start": v(-65.62, 37.89) * mm, "end": v(-65.62, -37.89) * mm});
            skLineSegment(sketch, "E245.1", {"start": v(65.62, -37.89) * mm, "end": v(0, -75.77) * mm});
            skLineSegment(sketch, "E245.2", {"start": v(65.62, -37.89) * mm, "end": v(65.62, 37.89) * mm});
            skLineSegment(sketch, "E245.3", {"start": v(-65.62, -37.89) * mm, "end": v(0, -75.77) * mm});
            skLineSegment(sketch, "E245.4", {"start": v(65.62, 37.89) * mm, "end": v(0, 75.77) * mm});
            skLineSegment(sketch, "E245.5", {"start": v(0, 75.77) * mm, "end": v(-65.62, 37.89) * mm});
            skEllipticalArc(sketch, "E246.0", {});
            skEllipticalArc(sketch, "E247.0", {});
            skEllipticalArc(sketch, "E248.0", {});
            skPoint(sketch, "E249.0.end.orphan", {"position": v(0.72, -55.97) * mm});
            skPoint(sketch, "E249.0.start.orphan", {"position": v(-2.2, -57.68) * mm});
            skArc(sketch, "E250.0", {"start": v(-6.91, -57.38) * mm, "mid": v(-3, -57.22) * mm, "end": v(0.72, -55.97) * mm});
            skArc(sketch, "E251.0", {"start": v(-43.5, 5.36) * mm, "mid": v(-37.25, 23.23) * mm, "end": v(-27.12, 39.23) * mm});
            skArc(sketch, "E252", {"start": v(-27.12, 39.23) * mm, "mid": v(-24.6, 42.2) * mm, "end": v(-21.96, 45.06) * mm, "construction": true});
            skArc(sketch, "E253", {"start": v(-21.96, 45.06) * mm, "mid": v(-15.1, 51.37) * mm, "end": v(-7.58, 56.88) * mm});
            skEllipticalArc(sketch, "E254", {"construction": true});
            skEllipticalArc(sketch, "E255", {});
            const initialGuessF6  = {"E246.0": [-0.011639922779706047, -0.02827968744979026, -0.8660254037844389, 0.5, 0.03596520862109229, 0.024357615432259415, 0, 2.2323374718868], "E247.0": [-0.011639922779706047, -0.02827968744979026, -0.8660254037844389, 0.5, 0.03596520862109229, 0.024357615432259415, 2.2323374718868, 2.3219350337154445], "E248.0": [-0.008122247099933005, -0.02456963054964719, 0.9624687106606815, -0.2713926693909868, 0.0439718499911378, 0.032099978341677673, 2.958237406010736, 5.052989680657434], "E254": [-0.022421108092777586, 0.040301324675147666, 0.6671519415157838, 0.7449216649633169, 0.0058095939473293105, 0.00378319059674068, 0.845184544428006, 2.313906359308788], "E255": [-0.022421108092777586, 0.040301324675147666, 0.6671519415157838, 0.7449216649633169, 0.0058095939473293105, 0.00378319059674068, 2.3139063593087874, 0.845184544428006]};
            skSetInitialGuess(sketch, initialGuessF6);
            skSolve(sketch);
        }
        {
            var Q0;
            Q0=makeQuery(id+"F6.imprint","IMPRINT",FACE,{"disambiguationData":[TD([[makeQuery(id+"F6.imprint","IMPRINT",EDGE,{"derivedFrom":sQuery(id+"F6.wireOp",EDGE,"E206.0")}),-1.0]])]});
            extrude(context, id + "F7", {"entities" : qUnion([Q0]), "depth" : 5 * mm, "offsetDistance" : 25 * mm});
        }
    });
